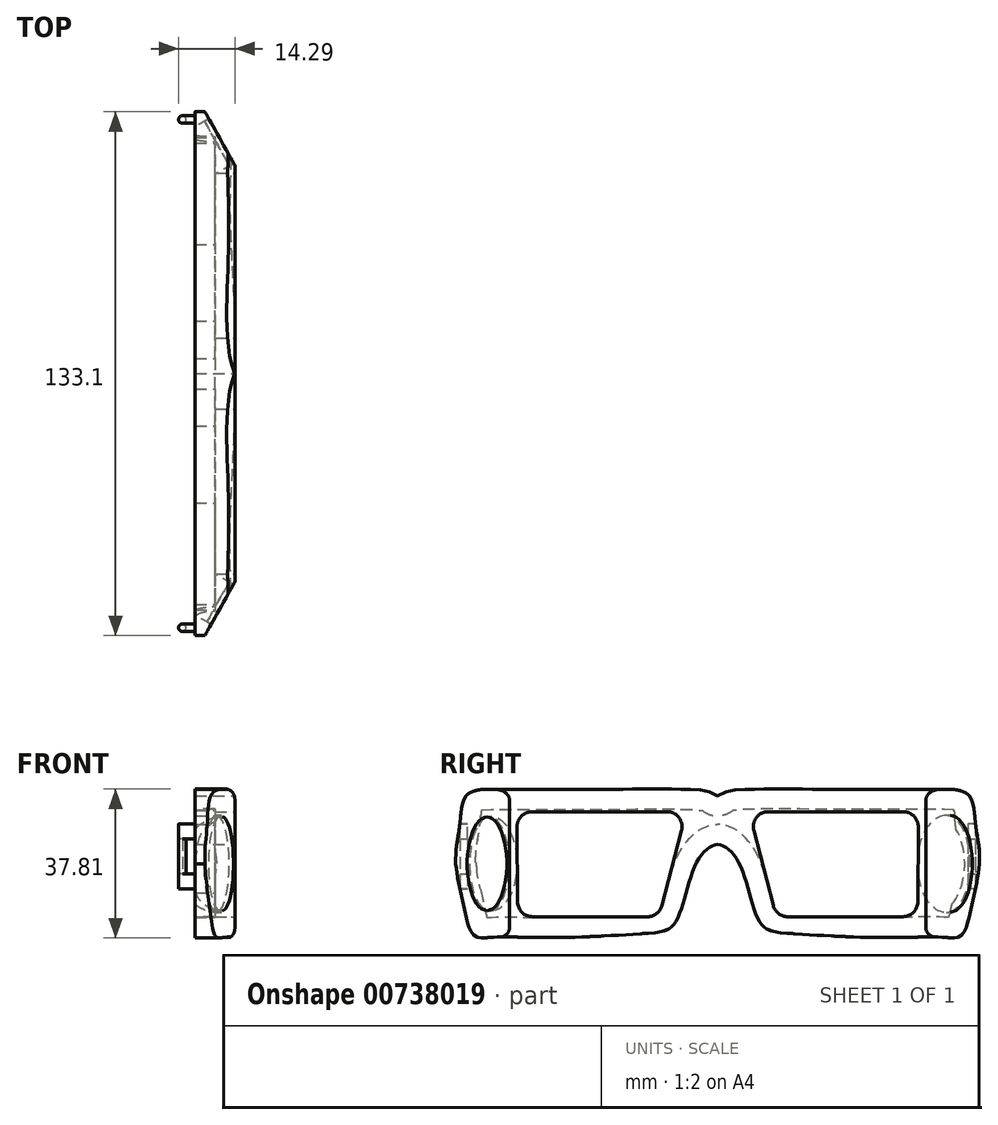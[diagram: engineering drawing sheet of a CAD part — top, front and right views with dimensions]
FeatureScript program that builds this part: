
annotation { "Feature Type Name" : "Feature", "Feature Type Description" : "" }
export const myFeature = defineFeature(function(context is Context, id is Id, definition is map)
    precondition{}
    {
        {
            var Q0;
            Q0=qCreatedBy(makeId("Front.planeOp"),FACE);
            var sketch = newSketch(context, id + "F0", { "sketchPlane" : qUnion([Q0])});
            skLineSegment(sketch, "E0.bottom", {"start": v(38.08, 38.1) * mm, "end": v(48.24, 38.1) * mm});
            skLineSegment(sketch, "E0.top", {"start": v(38.08, 0) * mm, "end": v(48.24, 0) * mm});
            skLineSegment(sketch, "E0.left", {"start": v(38.08, 38.1) * mm, "end": v(38.08, 0) * mm});
            skLineSegment(sketch, "E0.right", {"start": v(48.24, 38.1) * mm, "end": v(48.24, 0) * mm});
            skLineSegment(sketch, "E1", {"start": v(38.08, 38.1) * mm, "end": v(48.24, 36.3) * mm});
            skLineSegment(sketch, "E2", {"start": v(38.08, 0) * mm, "end": v(48.24, 1.8) * mm});
            skSolve(sketch);
        }
        {
            var Q0;
            Q0=makeQuery(id+"F0.imprint","IMPRINT",FACE,{"disambiguationData":[TD([[makeQuery(id+"F0.imprint","IMPRINT",EDGE,{"derivedFrom":sQuery(id+"F0.wireOp",EDGE,"E0.left")}),1.0]])]});
            var Q1;
            {var subQ0=sQuery(id+"F0.wireOp",EDGE,"E0.bottom");Q1=makeQuery(id+"F0.imprint","IMPRINT",FACE,{"disambiguationData":[TD([[makeQuery(id+"F0.imprint","IMPRINT",EDGE,{"derivedFrom":subQ0}),-1.0]])]});}
            var Q2;
            {var subQ0=sQuery(id+"F0.wireOp",EDGE,"E0.top");Q2=makeQuery(id+"F0.imprint","IMPRINT",FACE,{"disambiguationData":[TD([[makeQuery(id+"F0.imprint","IMPRINT",EDGE,{"derivedFrom":subQ0}),1.0]])]});}
            extrude(context, id + "F1", {"entities" : qUnion([Q0, Q1, Q2]), "endBound" : BoundingType.SYMMETRIC, "depth" : 133.35 * mm, "offsetDistance" : 25.4 * mm});
        }
        {
            var Q0;
            Q0=makeQuery(id+"F1.opExtrude","SWEPT_FACE",FACE,{"disambiguationData":[OSD([sQuery(id+"F0.wireOp",EDGE,"E0.right")])]});
            var sketch = newSketch(context, id + "F2", { "sketchPlane" : qUnion([Q0])});
            skPoint(sketch, "E3.7.internal.snap0", {"position": v(-66.68, 19.05) * mm});
            skLineSegment(sketch, "E4", {"start": v(0, 0) * mm, "end": v(0, 38.1) * mm, "construction": true});
            skFitSpline(sketch, "E5", {"points": [v(-66.55, 19.05) * mm, v(-65.71, 13.7) * mm, v(-64.65, 9.05) * mm, v(-62.03, 1) * mm, v(-57.55, 0.38) * mm, v(-41.4, 0.32) * mm, v(-17.74, 1.42) * mm, v(-10.9, 3.96) * mm, v(-5.52, 19.05) * mm, v(0, 23.99) * mm], "startDerivative": vector(9.32, -67.68) * mm, "endDerivative": vector(57.42, 1.11) * mm});
            skFitSpline(sketch, "E6", {"points": [v(-66.55, 19.05) * mm, v(-66.4, 23.22) * mm, v(-65.45, 29.69) * mm, v(-63.54, 36.74) * mm, v(-56.51, 37.96) * mm, v(-51.72, 37.99) * mm, v(-35.59, 37.9) * mm, v(-5.52, 37.86) * mm, v(-1.13, 36.93) * mm, v(0, 36.28) * mm], "startDerivative": vector(-0.25, 48.96) * mm, "endDerivative": vector(34.63, 0) * mm});
            skFitSpline(sketch, "E7.MirrorCS", {"points": [v(66.55, 19.05) * mm, v(66.4, 23.22) * mm, v(65.45, 29.69) * mm, v(63.54, 36.74) * mm, v(56.51, 37.96) * mm, v(51.72, 37.99) * mm, v(35.59, 37.9) * mm, v(5.52, 37.86) * mm, v(1.13, 36.93) * mm, v(0, 36.28) * mm], "startDerivative": vector(0.25, 48.96) * mm, "endDerivative": vector(-34.63, 0) * mm});
            skFitSpline(sketch, "E8.MirrorCS", {"points": [v(66.55, 19.05) * mm, v(65.71, 13.7) * mm, v(64.65, 9.05) * mm, v(62.03, 1) * mm, v(57.55, 0.38) * mm, v(41.4, 0.32) * mm, v(17.74, 1.42) * mm, v(10.9, 3.96) * mm, v(5.52, 19.05) * mm, v(0, 23.99) * mm], "startDerivative": vector(-9.32, -67.68) * mm, "endDerivative": vector(-57.42, 1.11) * mm});
            skSolve(sketch);
        }
        {
            var Q0;
            Q0=makeQuery(id+"F1.opExtrude","SWEPT_EDGE",EDGE,{"disambiguationData":[OSD([sQuery(id+"F0.wireOp",EDGE,"E0.right"),sQuery(id+"F0.wireOp",EDGE,"E1")])]});
            var Q1;
            Q1=makeQuery(id+"F1.opExtrude","SWEPT_EDGE",EDGE,{"disambiguationData":[OSD([sQuery(id+"F0.wireOp",EDGE,"E0.right"),sQuery(id+"F0.wireOp",EDGE,"E2")])]});
            fillet(context, id + "F3", {"entities" : qUnion([Q0, Q1]), "radius" : 2.54 * mm, "tangentPropagation" : true, "allowEdgeOverflow" : false});
        }
        {
            var Q0;
            Q0=makeQuery(id+"F2.imprint","IMPRINT",FACE,{"disambiguationData":[TD([[makeQuery(id+"F2.imprint","IMPRINT",EDGE,{"derivedFrom":sQuery(id+"F2.wireOp",EDGE,"E5")}),-1.0]])]});
            extrude(context, id + "F4", {"entities" : qUnion([Q0]), "operationType" : NewBodyOperationType.REMOVE, "oppositeDirection" : true, "depth" : 25.4 * mm, "offsetDistance" : 25.4 * mm});
        }
        {
            var Q0;
            Q0=makeQuery(id+"F1.opExtrude","SWEPT_FACE",FACE,{"disambiguationData":[OSD([sQuery(id+"F0.wireOp",EDGE,"E0.left")])]});
            shell(context, id + "F5", {"entities" : qUnion([Q0]), "thickness" : 5.08 * mm});
        }
        {
            var Q0;
            Q0=makeQuery(id+"F1.opExtrude","SWEPT_FACE",FACE,{"disambiguationData":[OSD([sQuery(id+"F0.wireOp",EDGE,"E0.right")])]});
            var sketch = newSketch(context, id + "F6", { "sketchPlane" : qUnion([Q0])});
            skLineSegment(sketch, "E9", {"start": v(-17.82, 5.62) * mm, "end": v(-47.03, 5.62) * mm});
            skLineSegment(sketch, "E10", {"start": v(-50.84, 9.4) * mm, "end": v(-50.96, 28.46) * mm});
            skLineSegment(sketch, "E11", {"start": v(-47.15, 32.3) * mm, "end": v(-12.86, 32.3) * mm});
            skLineSegment(sketch, "E12", {"start": v(-9.17, 27.52) * mm, "end": v(-14.13, 8.47) * mm});
            skPoint(sketch, "E13.visualSharp", {"position": v(-50.98, 32.3) * mm});
            skArc(sketch, "E13.filletArc", {"start": v(-47.15, 32.3) * mm, "mid": v(-49.85, 31.17) * mm, "end": v(-50.96, 28.46) * mm});
            skPoint(sketch, "E14.visualSharp", {"position": v(-7.93, 32.3) * mm});
            skArc(sketch, "E14.filletArc", {"start": v(-9.17, 27.52) * mm, "mid": v(-9.84, 30.81) * mm, "end": v(-12.86, 32.3) * mm});
            skPoint(sketch, "E15.visualSharp", {"position": v(-14.87, 5.62) * mm});
            skArc(sketch, "E15.filletArc", {"start": v(-17.82, 5.62) * mm, "mid": v(-15.49, 6.42) * mm, "end": v(-14.13, 8.47) * mm});
            skPoint(sketch, "E16.visualSharp", {"position": v(-50.81, 5.62) * mm});
            skArc(sketch, "E16.filletArc", {"start": v(-50.84, 9.4) * mm, "mid": v(-49.71, 6.73) * mm, "end": v(-47.03, 5.62) * mm});
            skLineSegment(sketch, "E17.0", {"start": v(0, 0) * mm, "end": v(0, 38.1) * mm, "construction": true});
            skLineSegment(sketch, "E18.MirrorCS", {"start": v(47.15, 32.3) * mm, "end": v(12.86, 32.3) * mm});
            skArc(sketch, "E19.MirrorCS", {"start": v(9.17, 27.52) * mm, "mid": v(9.84, 30.81) * mm, "end": v(12.86, 32.3) * mm});
            skLineSegment(sketch, "E20.MirrorCS", {"start": v(9.17, 27.52) * mm, "end": v(14.13, 8.47) * mm});
            skArc(sketch, "E21.MirrorCS", {"start": v(17.82, 5.62) * mm, "mid": v(15.49, 6.42) * mm, "end": v(14.13, 8.47) * mm});
            skLineSegment(sketch, "E22.MirrorCS", {"start": v(17.82, 5.62) * mm, "end": v(47.03, 5.62) * mm});
            skArc(sketch, "E23.MirrorCS", {"start": v(50.84, 9.4) * mm, "mid": v(49.71, 6.73) * mm, "end": v(47.03, 5.62) * mm});
            skLineSegment(sketch, "E24.MirrorCS", {"start": v(50.84, 9.4) * mm, "end": v(50.96, 28.46) * mm});
            skArc(sketch, "E25.MirrorCS", {"start": v(47.15, 32.3) * mm, "mid": v(49.85, 31.17) * mm, "end": v(50.96, 28.46) * mm});
            skSolve(sketch);
        }
        {
            var Q0;
            Q0 = qSketchRegion(id + "F6", true);
            extrude(context, id + "F7", {"entities" : qUnion([Q0]), "operationType" : NewBodyOperationType.REMOVE, "endBound" : BoundingType.THROUGH_ALL, "oppositeDirection" : true, "depth" : 25.4 * mm, "offsetDistance" : 25.4 * mm});
        }
        {
            var Q0;
            Q0=qCreatedBy(makeId("Top.planeOp"),FACE);
            var sketch = newSketch(context, id + "F8", { "sketchPlane" : qUnion([Q0])});
            skLineSegment(sketch, "E26.3", {"start": v(48.24, 64.42) * mm, "end": v(48.24, -64.42) * mm});
            skLineSegment(sketch, "E26.4", {"start": v(38.08, 0) * mm, "end": v(48.24, 0) * mm});
            skLineSegment(sketch, "E27", {"start": v(48.24, 66.55) * mm, "end": v(48.24, 64.42) * mm});
            skLineSegment(sketch, "E28.0", {"start": v(43.16, 50.84) * mm, "end": v(48.24, 50.84) * mm});
            skLineSegment(sketch, "E29", {"start": v(40.62, 66.57) * mm, "end": v(48.24, 52.94) * mm});
            skLineSegment(sketch, "E30", {"start": v(48.24, 66.55) * mm, "end": v(48.24, 67.01) * mm});
            skLineSegment(sketch, "E31", {"start": v(48.24, 67.01) * mm, "end": v(37.33, 67.01) * mm});
            skLineSegment(sketch, "E32", {"start": v(40.62, 66.57) * mm, "end": v(40.38, 67.01) * mm});
            skLineSegment(sketch, "E33.MirrorCS", {"start": v(48.24, -66.55) * mm, "end": v(48.24, -64.42) * mm});
            skLineSegment(sketch, "E34.MirrorCS", {"start": v(48.24, -64.42) * mm, "end": v(48.24, 64.42) * mm});
            skLineSegment(sketch, "E35.MirrorCS", {"start": v(40.62, -66.57) * mm, "end": v(48.24, -52.94) * mm});
            skLineSegment(sketch, "E36.MirrorCS", {"start": v(48.24, -67.01) * mm, "end": v(37.33, -67.01) * mm});
            skLineSegment(sketch, "E37.MirrorCS", {"start": v(40.62, -66.57) * mm, "end": v(40.38, -67.01) * mm});
            skLineSegment(sketch, "E38", {"start": v(48.24, -66.55) * mm, "end": v(48.24, -67.01) * mm});
            skSolve(sketch);
        }
        {
            var Q0;
            Q0 = qSketchRegion(id + "F8", true);
            extrude(context, id + "F9", {"entities" : qUnion([Q0]), "operationType" : NewBodyOperationType.REMOVE, "endBound" : BoundingType.THROUGH_ALL, "depth" : 25.4 * mm, "offsetDistance" : 25.4 * mm});
        }
        {
            var Q0;
            Q0=makeQuery(id+"F9.boolean.opBoolean","COPY",FACE,{"derivedFrom":makeQuery(id+"F9.opExtrude","SWEPT_FACE",FACE,{"disambiguationData":[OSD([sQuery(id+"F8.wireOp",EDGE,"E29"),sQuery(id+"F8.wireOp",EDGE,"E32")])]})});
            var sketch = newSketch(context, id + "F10", { "sketchPlane" : qUnion([Q0])});
            skEllipse(sketch, "E39", {"center": v(29.7, 19.05) * mm, "majorRadius": 12.31 * mm, "minorRadius": 6.52 * mm, "majorAxis": v(0, -1)});
            skPoint(sketch, "E39.centerSnap0", {"position": v(22.68, 19.05) * mm});
            skSolve(sketch);
        }
        {
            var Q0;
            Q0 = qSketchRegion(id + "F10", true);
            extrude(context, id + "F11", {"entities" : qUnion([Q0]), "operationType" : NewBodyOperationType.REMOVE, "endBound" : BoundingType.THROUGH_ALL, "oppositeDirection" : true, "depth" : 25.4 * mm, "offsetDistance" : 25.4 * mm});
        }
        {
            var Q0;
            Q0 = qSketchRegion(id + "F10", true);
            extrude(context, id + "F12", {"entities" : qUnion([Q0]), "oppositeDirection" : true, "depth" : 1.27 * mm, "offsetDistance" : 25.4 * mm});
        }
        {
            var Q0;
            Q0=makeQuery(id+"F9.boolean.opBoolean","COPY",FACE,{"derivedFrom":makeQuery(id+"F9.opExtrude","SWEPT_FACE",FACE,{"disambiguationData":[OSD([sQuery(id+"F8.wireOp",EDGE,"E35.MirrorCS"),sQuery(id+"F8.wireOp",EDGE,"E37.MirrorCS")])]})});
            var sketch = newSketch(context, id + "F13", { "sketchPlane" : qUnion([Q0])});
            skEllipse(sketch, "E40", {"center": v(-29.17, 19.05) * mm, "majorRadius": 11.94 * mm, "minorRadius": 5.8 * mm, "majorAxis": v(0, -1)});
            skPoint(sketch, "E40.centerSnap0", {"position": v(-22.68, 19.05) * mm});
            skSolve(sketch);
        }
        {
            var Q0;
            Q0 = qSketchRegion(id + "F13", true);
            extrude(context, id + "F14", {"entities" : qUnion([Q0]), "operationType" : NewBodyOperationType.REMOVE, "endBound" : BoundingType.THROUGH_ALL, "oppositeDirection" : true, "depth" : 25.4 * mm, "offsetDistance" : 25.4 * mm});
        }
        {
            var Q0;
            Q0 = qSketchRegion(id + "F13", true);
            extrude(context, id + "F15", {"entities" : qUnion([Q0]), "oppositeDirection" : true, "depth" : 1.27 * mm, "offsetDistance" : 25.4 * mm});
        }
        {
            var Q0;
            Q0=qCreatedBy(makeId("Top.planeOp"),FACE);
            var sketch = newSketch(context, id + "F16", { "sketchPlane" : qUnion([Q0])});
            skFitSpline(sketch, "E41.0", {"points": [v(38.08, -66.55) * mm, v(38.08, -66.3) * mm, v(38.08, -65.79) * mm, v(38.08, -64.6) * mm, v(38.08, -62.97) * mm, v(38.08, -56.8) * mm, v(38.08, -41.24) * mm, v(38.08, -18.24) * mm, v(38.08, -9.3) * mm, v(38.08, -7.12) * mm, v(38.08, -1.87) * mm, v(38.08, 0) * mm]});
            skLineSegment(sketch, "E42.0", {"start": v(38.08, 0) * mm, "end": v(48.24, 0) * mm});
            skPoint(sketch, "E43.0", {"position": v(38.08, -61.47) * mm});
            skPoint(sketch, "E44.0", {"position": v(38.08, -66.55) * mm});
            skLineSegment(sketch, "E45", {"start": v(38.08, -63.61) * mm, "end": v(34.9, -63.61) * mm});
            skLineSegment(sketch, "E46", {"start": v(38.08, -65.52) * mm, "end": v(34.9, -65.52) * mm});
            skLineSegment(sketch, "E47", {"start": v(34.9, -65.52) * mm, "end": v(34.9, -63.61) * mm, "construction": true});
            skLineSegment(sketch, "E48", {"start": v(38.08, -65.52) * mm, "end": v(38.08, -63.61) * mm});
            skCircle(sketch, "E49", {"center": v(34.9, -64.57) * mm, "radius": 0.95 * mm});
            skFitSpline(sketch, "E50.MirrorCS", {"points": [v(38.08, 66.55) * mm, v(38.08, 66.3) * mm, v(38.08, 65.79) * mm, v(38.08, 64.6) * mm, v(38.08, 62.97) * mm, v(38.08, 56.8) * mm, v(38.08, 41.24) * mm, v(38.08, 18.24) * mm, v(38.08, 9.3) * mm, v(38.08, 7.12) * mm, v(38.08, 1.87) * mm, v(38.08, 0) * mm]});
            skLineSegment(sketch, "E51.MirrorCS", {"start": v(38.08, 65.52) * mm, "end": v(38.08, 63.61) * mm});
            skLineSegment(sketch, "E52.MirrorCS", {"start": v(38.08, 65.52) * mm, "end": v(34.9, 65.52) * mm});
            skLineSegment(sketch, "E53.MirrorCS", {"start": v(38.08, 63.61) * mm, "end": v(34.9, 63.61) * mm});
            skCircle(sketch, "E54.MirrorC", {"center": v(34.9, 64.57) * mm, "radius": 0.95 * mm});
            skLineSegment(sketch, "E55.MirrorCS", {"start": v(34.9, 65.52) * mm, "end": v(34.9, 63.61) * mm, "construction": true});
            skSolve(sketch);
        }
        {
            var Q0;
            {var subQ0=sQuery(id+"F16.wireOp",EDGE,"E54.MirrorC");var subQ1=makeQuery(id+"F16.imprint","INTERSECT",VERTEX,{"derivedFrom":[sQuery(id+"F16.wireOp",EDGE,"E52.MirrorCS"),subQ0]});Q0=makeQuery(id+"F16.imprint","IMPRINT",FACE,{"disambiguationData":[TD([[makeQuery(id+"F16.imprint","IMPRINT",EDGE,{"disambiguationData":[TD([[subQ1,1.0]])],"derivedFrom":subQ0}),-1.0]])]});}
            var Q1;
            {var subQ0=sQuery(id+"F16.wireOp",EDGE,"E49");var subQ1=makeQuery(id+"F16.imprint","INTERSECT",VERTEX,{"derivedFrom":[sQuery(id+"F16.wireOp",EDGE,"E45"),subQ0]});Q1=makeQuery(id+"F16.imprint","IMPRINT",FACE,{"disambiguationData":[TD([[makeQuery(id+"F16.imprint","IMPRINT",EDGE,{"disambiguationData":[TD([[subQ1,-1.0]])],"derivedFrom":subQ0}),1.0]])]});}
            extrude(context, id + "F17", {"entities" : qUnion([Q0, Q1]), "operationType" : NewBodyOperationType.ADD, "depth" : 29.2 * mm, "offsetDistance" : 25.4 * mm});
        }
        {
            var Q0;
            Q0 = qSketchRegion(id + "F16", true);
            var Q1;
            Q1=makeQuery(id+"F17.opExtrude","CAP_FACE",FACE,{"disambiguationData":[OSD([sQuery(id+"F16.wireOp",EDGE,"E49")])],"isStart":true});
            extrude(context, id + "F18", {"entities" : qUnion([Q0, Q1]), "operationType" : NewBodyOperationType.ADD, "depth" : 16.5 * mm, "offsetDistance" : 25.4 * mm});
        }
        {
            var Q0;
            Q0 = qSketchRegion(id + "F16", true);
            extrude(context, id + "F19", {"entities" : qUnion([Q0]), "operationType" : NewBodyOperationType.REMOVE, "depth" : 12.7 * mm, "offsetDistance" : 25.4 * mm});
        }
        {
            var Q0;
            Q0=makeQuery(id+"F17.opExtrude","CAP_FACE",FACE,{"disambiguationData":[OSD([sQuery(id+"F16.wireOp",EDGE,"E54.MirrorC")])],"isStart":false});
            var sketch = newSketch(context, id + "F20", { "sketchPlane" : qUnion([Q0])});
            skLineSegment(sketch, "E56.0", {"start": v(38.08, 0) * mm, "end": v(48.14, 0) * mm});
            skCircle(sketch, "E57.0", {"center": v(34.9, 64.57) * mm, "radius": 0.95 * mm});
            skLineSegment(sketch, "E57.1", {"start": v(38.08, 65.52) * mm, "end": v(34.9, 65.52) * mm});
            skLineSegment(sketch, "E57.2", {"start": v(38.08, 63.61) * mm, "end": v(34.9, 63.61) * mm});
            skLineSegment(sketch, "E57.3", {"start": v(38.08, 65.52) * mm, "end": v(38.08, 63.61) * mm});
            skCircle(sketch, "E58.MirrorC", {"center": v(34.9, -64.57) * mm, "radius": 0.95 * mm});
            skLineSegment(sketch, "E59.MirrorCS", {"start": v(38.08, -63.61) * mm, "end": v(34.9, -63.61) * mm});
            skLineSegment(sketch, "E60.MirrorCS", {"start": v(38.08, -65.52) * mm, "end": v(38.08, -63.61) * mm});
            skLineSegment(sketch, "E61.MirrorCS", {"start": v(38.08, -65.52) * mm, "end": v(34.9, -65.52) * mm});
            skSolve(sketch);
        }
        {
            var Q0;
            Q0 = qSketchRegion(id + "F20", true);
            extrude(context, id + "F21", {"entities" : qUnion([Q0]), "operationType" : NewBodyOperationType.ADD, "oppositeDirection" : true, "depth" : 3.8 * mm, "offsetDistance" : 25.4 * mm});
        }
    });
